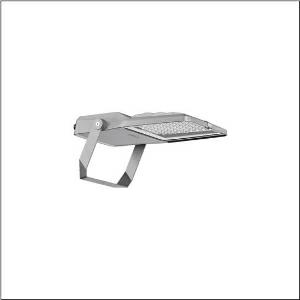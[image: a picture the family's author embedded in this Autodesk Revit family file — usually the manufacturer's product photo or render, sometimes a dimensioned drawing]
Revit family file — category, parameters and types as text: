
# Revit family: floodlight_fl_21_iq_mini___pl52_5xa7772d1d1a_9c36
name_source: partatom
category: Lighting Fixtures
units: mm (PartAtom-declared; Revit-internal decimal feet)

## family parameters
Cut with Voids When Loaded = No
Host = Face
Light Source = No
Part Type = Normal
Room Calculation Point = No
Round Connector Dimension = Use Diameter
Shared = No

## types (1)
- --- (1 x LED, 14760 lm, 143 W, 2200K)
    Apparent Load = 143 VA
    CIE Flux Codes = 26 60 98 100 100
    Color Rendering = 70
    Color Temperature = 2200K
    Default Elevation = 1800 mm
    Description = Floodlight FL 21 iQ mini, floodlight, primary light control with lens, of PMMA, primary optical cover: protective disc, of toughened safety glass, transparent, light distribution: PL52, light emission: direct distribution, installation type: surface-mounted, lamps: LED, High Power LED, rated values: 14.760lm | 143W | 103,2lm/W (begin service life); end service life: 14.760lm | 151,6W; at 50% lumin. flux: 7.380lm | 60,5W | 122lm/W, colour temperature: 2200K, colour rendering: CRI > 70, light colour: 722, light setting 1 begin service life: 100% | 14.760lm | 143W | 103,2lm/W | 2.200K, light setting 1 end service life: 151,6W, further light settings possible, control: Street-Remote, Auto-Match, Temp-Guard, Night-Set, Smart-Wire, Desk-Remote (wireless, voltage-free reading and setting of iQ features in the workshop via application-optimized NFC function/RFID function), optimised constant luminous flux control (CLO 2.0), pre-setting: linear dimming characteristic, with terminal, 6-pole, mains connection: 220..240V, AC, 50/60Hz, luminaire housing, of diecast aluminium, powder-coated, SITECO metallic grey (DB 702S), corrosivity category C5 mid according to DIN EN ISO 12944suitable for swimming poolschlorine-resistant, sealing non-destructively replaceable, mounting bracket, of steel, galvanised, powder-coated, SITECO metallic grey (DB 702S), protection rating (complete): IP66, insulation class (complete): insulation class II (safety insulation), certification: CE, ENEC, VDE, protection symbol: D, impact resistance: IK08, permissible operating ambient temperature: -40..+40°C, permissible operating ambient temperature for outdoor applications: -40..+50°C, standard: DIN EN 12944, LABS conformity tested according to VDMA 24364:2018-05, packaging unit: 1 piece

Light Distribution: PL52
    Height = 70 mm
    Lamp = 1 x LED
    Lamp Light Flux = 14760 lm
    Lamp Power = 143 W
    Lamp count = 1
    Length = 485 mm
    Luminous efficacy = 103 lm/W
    Manufacturer = Siteco
    ModVariant = No
    Model = 5XA7772D1D1A
    Number of Poles = 1
    OnlyDefault = Yes
    Power Factor = 1
    Product Name = Floodlight FL 21 iQ mini | PL52
    Product group = floodlight | pylon annexe
    ProductGroupID = 6201
    Protection Class = Protection class II
    Protection Degree = IP 66
    RLX_Detail_Level = 1
    RLX_Emergency_Light_Flux = 0 lm
    RLX_Emergency_Type = 0
    RLX_Emergency_Type_DB = No
    RlxData = <blob elided: 96849 chars, md5=02d52ced>
    Socket = socket
    Standby Power = 0 W
    System Light Flux = 14760 lm
    System Power = 143 W
    Type Comments = factory setting: luminous flux: 100 % | dim-lin: 254 | 730 mA
    Type Image = l_1006845.jpg
    URL = http://relux.com
    VarID = @adj_163295
    Voltage = 0 V
    Weight = 0.00 kg
    Width = 337 mm

## geometry (parser evidence)
native form markers: Blend x4, Sweep x13
no freeform markers — native parametric forms only
